# Revit family: 3079453 Feilo Sylvania Lighting Fixture INST ECO KIT LED ADJ WH NW DIMMABLE
name_source: partatom
category: Lighting Fixtures
revit_build: Autodesk Revit 2017 (Build: 20190507_1515(x64)
units: mm (PartAtom-declared; Revit-internal decimal feet)

## family parameters
Cut with Voids When Loaded = No
Host = Face
Light Source = No
OmniClass Number = 23.80.70.11.17
OmniClass Title = Specialized Lighting by Location or Use
Part Type = Normal
Room Calculation Point = No
Round Connector Dimension = Use Diameter
Shared = No

## types (1)
- 3079453 INST ECO KIT LED ADJ WH NW DIMMABLE
    AccessoryBodyInnerDiameter_FEILO = 60 mm  [stored 0.19685 ft]
    AccessoryBodyOuterDiameter_FEILO = 63.5 mm  [stored 0.208333 ft]
    AccessoryInnerDiameter_FEILO = 49.5 mm  [stored 0.162402 ft]
    AccessoryOuterDiameter_FEILO = 78 mm  [stored 0.255906 ft]
    Apparent Load = 10 VA
    Assembly Code = D5020200
    AssetType = Fixed
    CutoutDiameter_FEILO = 68 mm
    Default Elevation = 0 mm  [stored 0 ft]
    Description = Utilsing SunDim technology to acheive warmer colour temperature as the fitting is dimmed. Incredible colour quality with 92  to 94 CRI. 12W LED white downlight. Ideal for hospitality accent and display lighting applications such as bathrooms, wellness areas, terraces or porches. Choice of fixed, adjustable and dimmable fixed versions. Comes complete and ready to install with its driver. Available in white and brushed aluminium finishes. Outstanding performace, up to 545lm - at 3,000K. A small 68mm round cut out is required, giving the ability to place your light source almost anywhere due to a shallow luminaire depth of 49.9mm. Quick and easy to install. No UV or IR radiations. LED technology provides energy efficient solution and reduced maintenance costs
    Diameter_FEILO = 78 mm  [stored 0.255906 ft]
    DimmingControlOptions = Dimmable
    DocumentationLiterature = http://www.sylvania-lighting.com
    DurationUnit = hours
    ElectricShockClassification = Class II
    ExpectedLife = 50000
    HeadDiameter_FEILO = 48 mm  [stored 0.15748 ft]
    HeadRadius_FEILO = 24 mm  [stored 0.0787402 ft]
    Height_FEILO = 62 mm  [stored 0.203412 ft]
    IfcExportAs = IfcLightFixtureType
    IfcExportType = IfcLightFixtureType
    ImpactProtectionIndex = IK02
    IngressProtection = IP23
    InputVoltage = 220-240V~
    Keynote = 16500
    Lamp = LED
    LampColourRenderingIndex = 83
    LampColourTemperature = 4000 K
    LampNominalLuminous = 515 lm
    LampsType = LED
    LightOutputRatio = 100
    LuminousEfficacy = 51.5 lm/W
    Manufacturer = Feilo Sylvania
    ManufacturerName = Feilo Sylvania
    Material = aluminium housing, plastic diffuser
    Material_1_FEILO = Aluminum_Sylvania_Instar Eco Kit Adjustable SunDim_Bright
    Material_2_FEILO = Aluminum_Sylvania_Instar Eco Kit Adjustable SunDim_White
    Material_3_FEILO = Aluminum_Sylvania_Instar Eco Kit Adjustable SunDim_White
    Material_4_FEILO = Glass_Sylvania_Instar Eco Kit Adjustable SunDim_Clear
    Model = INST ECO KIT LED ADJ WH NW DIMMABLE
    ModelNumber = 3079453
    ModelReference = INST ECO KIT LED ADJ WH NW DIMMABLE
    Name = INST ECO KIT LED ADJ WH NW DIMMABLE
    NominalHeight = 62 mm  [stored 0.203412 ft]
    NominalLength = 78 mm  [stored 0.255906 ft]
    NominalWidth = 0 mm  [stored 0 ft]
    Offset_FEILO = -5.3 mm
    PowerConsumption = 10 W
    PowerFactor = 0
    RecessedDepth_FEILO = 100 mm  [stored 0.328084 ft]
    TypeHead_FEILO = Rotateable Head : 3079453 INST ECO KIT LED ADJ WH NW DIMMABLE
    TypeName = INST ECO KIT LED ADJ WH NW DIMMABLE
    URL = http://www.sylvania-lighting.com
    Voltage = 230 V
    Weight = 7.04 kg

note: [stored X ft] marks values corroborated as IEEE doubles in the binary element streams (Revit-internal decimal feet)

## geometry (parser evidence)
native form markers: Sweep x5
no freeform markers — native parametric forms only
